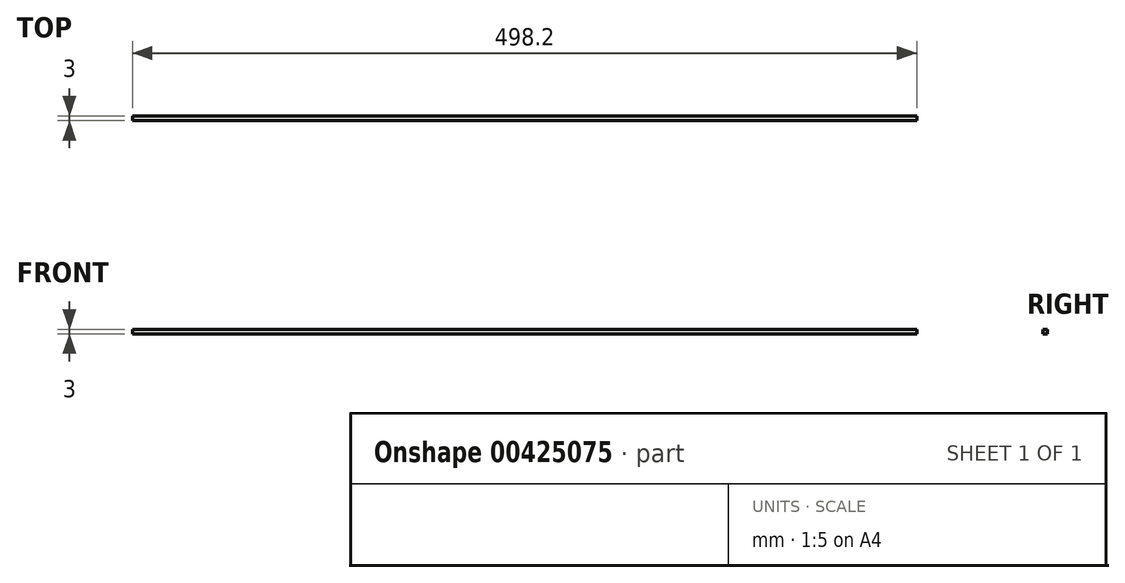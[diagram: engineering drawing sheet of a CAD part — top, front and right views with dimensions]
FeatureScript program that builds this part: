
annotation { "Feature Type Name" : "Feature", "Feature Type Description" : "" }
export const myFeature = defineFeature(function(context is Context, id is Id, definition is map)
    precondition{}
    {
        {
            var Q0;
            Q0=qCreatedBy(makeId("Top.planeOp"),FACE);
            var sketch = newSketch(context, id + "F0", { "sketchPlane" : qUnion([Q0])});
            skLineSegment(sketch, "E0.bottom", {"start": v(-252.05, 3) * mm, "end": v(246.15, 3) * mm});
            skLineSegment(sketch, "E0.top", {"start": v(-252.05, 0) * mm, "end": v(246.15, 0) * mm});
            skLineSegment(sketch, "E0.left", {"start": v(-252.05, 3) * mm, "end": v(-252.05, 0) * mm});
            skLineSegment(sketch, "E0.right", {"start": v(246.15, 3) * mm, "end": v(246.15, 0) * mm});
            skSolve(sketch);
        }
        {
            var Q0;
            Q0 = qSketchRegion(id + "F0", true);
            extrude(context, id + "F1", {"entities" : qUnion([Q0]), "depth" : 3 * mm});
        }
    });
